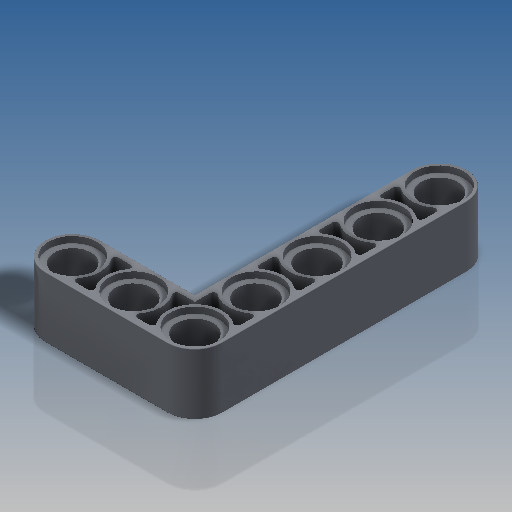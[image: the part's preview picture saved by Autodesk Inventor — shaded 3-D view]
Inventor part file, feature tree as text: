
AUTODESK INVENTOR PART (.ipt)
format: ipt  version: 2019.4 (Build 234330000, 330)  size: 437,248 bytes
history: native  units: mm
features: extrude x3, sketch x2, mirror x1, fillet x1
ambient origin geometry x8: Origin, YZ Plane, XZ Plane, XY Plane, X Axis, Y Axis, Z Axis, Center Point
bodies: Solid1 (feature_tree)
feature tree (7):
  extrude  "Extrusion1"  Depth=6.4mm
  sketch  "Sketch6"  dims[d14=8.0mm d15=0.0mm d32=7.2mm d34=8.0mm d36=0.8mm d41=0.8mm d42=0.0mm d43=3.1mm d44=0.0mm d46=0.4mm d47=0.1mm d49=0.8mm]
  extrude  "Extrusion7"  Depth=7.2mm
  extrude  "Extrusion8"  Depth=8.0mm
  mirror  "Mirror1"
  fillet  "Fillet1"  Radius=0.8mm
  sketch  "Sketch1"  dims[d8=4.8mm d9=6.4mm]
